# Revit family: FIRECLASS ESSENTIAL 2 ZONE PANEL
name_source: partatom
category: Electrical Equipment
revit_build: Autodesk Revit 2018 (Build: 20170223_1515(x64)
units: mm (PartAtom-declared; Revit-internal decimal feet)

## family parameters
Always vertical = Yes
Cut with Voids When Loaded = No
Host = Wall
Panel Configuration = Two Columns, Circuits Across
Part Type = Panelboard
Room Calculation Point = No
Round Connector Dimension = Use Diameter
Shared = No

## types (1)
- Essential 2 Zone Panel
    Brand = FireClass
    COBie.Type.AssetType = Moveable
    COBie.Type.Category = Ee_40_15_75
    COBie.Type.CodePerformance = EN 54-2, EN 54-4, Part of EN 54-13 System
    COBie.Type.Colour = RAL 7035
    COBie.Type.Description = FireClass Essential 2 Zone Conventional Panel
    COBie.Type.DurationUnit = Year
    COBie.Type.Features = Delay, Day and Night Mode
    COBie.Type.Manufacturer = www.fireclass.com
    COBie.Type.Material = Plastic (PC-ABS)
    COBie.Type.ModelNumber = Essential 2 Zone Panel
    COBie.Type.Name = FireClass Essential 2 Zone Panel
    COBie.Type.NominalHeight = 282 mm
    COBie.Type.NominalLength = 352 mm  [stored 1.15486 ft]
    COBie.Type.NominalWidth = 86 mm  [stored 0.282152 ft]
    COBie.Type.Shape = Rectangle
    COBie.Type.WarrantyDescription = The 36 month warranty is applicable from the date of manufacture.
    COBie.Type.WarrantyDurationLabor = 3
    COBie.Type.WarrantyDurationParts = 3
    COBie.Type.WarrantyDurationUnit = Year
    Description = FireClass Essential 2 Zone Panel
    Devices Per Zone = 32
    Electrical Device Nominal Power = 50W
    Has Protective Earth = TRUE
    Height = 282 mm
    IP_Code = IP 30
    Installation Date = 1900-12-31T23:59:59
    Length = 352 mm  [stored 1.15486 ft]
    Manufacturer = Tyco Fire & Security GmbH
    Manufacturer Name = Tyco Fire & Security GmbH
    Manufacturer URL = www.fireclass.net
    Model = Essential 2 Zone Panel
    NBS Description = Fire detection and alarm control and indicating equipment (CIE)
    NBS Reference = 90-75-30/380
    No Of Zonal LEDs = 4
    No Of Zones Supported = 2
    Nominal Current = 0.65 A
    Nominal Frequency Range = 50 Hz
    Nominal Voltage = 230 V AC
    Number of Zones = 2
    Operation Temperature Range = -5 °C to +40 °C
    Product Codes = 508.032.730
    Product Information = https://docs.jci.com
    Product Specification = FireClass Essential 2 Zone low-cost Conventional Panel with maximum 64 devices - 32 per each zone,  Simple user interface with icons, 2 zones and 22 LEDs for visual indication. Compact plastic housing, 1.8A PSU, 2 x 12 V, 3.4Ah batteries.
    Relative Humidity = 90% RH continuous (non-condensing)
    Room Tag = [Enter Tag Here]
    Show Room Tag = No
    Storage Temperature = -20 °C to +70 °C
    Total No Of Devices = 64
    URL = www.fireclass.net
    Uniclass2 = Ee_40_15_75
    Version = 1
    Warranty Start Date = 1900-12-31T23:59:59
    Weight = 2.15 kg
    Width = 86 mm  [stored 0.282152 ft]
    Zone Panels = 2

note: [stored X ft] marks values corroborated as IEEE doubles in the binary element streams (Revit-internal decimal feet)

## geometry (parser evidence)
native form markers: Sweep x5
no freeform markers — native parametric forms only
